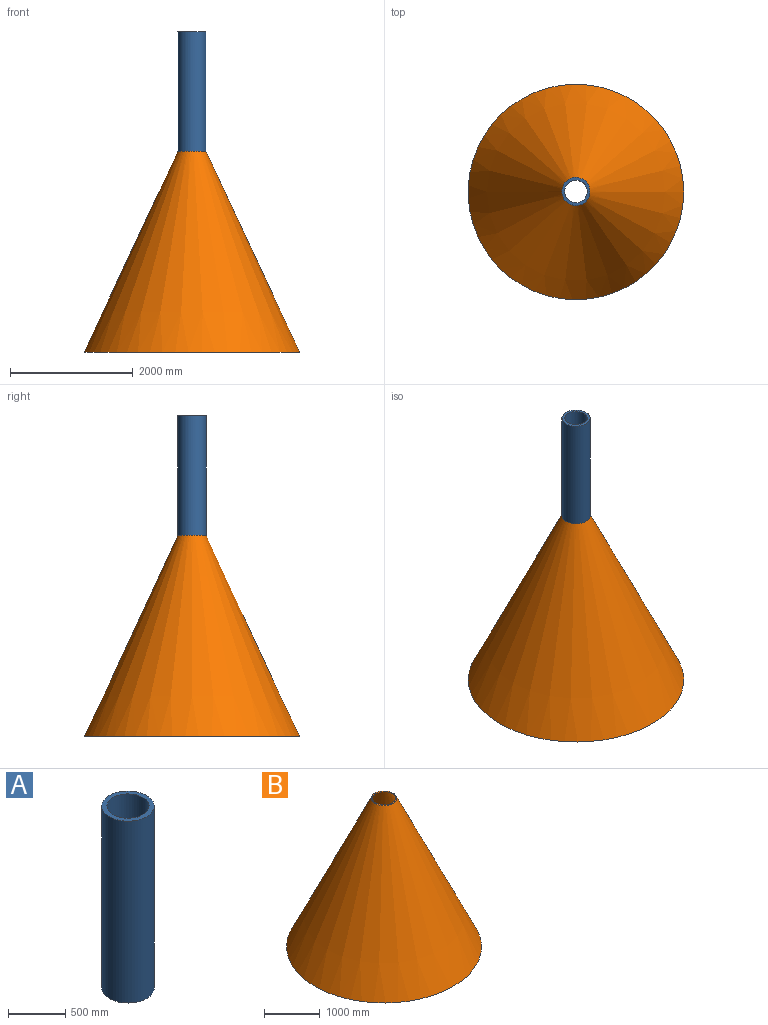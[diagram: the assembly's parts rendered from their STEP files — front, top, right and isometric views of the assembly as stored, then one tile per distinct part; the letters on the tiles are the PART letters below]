
ASSEMBLY  parts=2 mates=1
PART A: 4 faces, bbox 457.2x457.2x1945 mm
  f0: cylinder r=183.6mm len=1945mm, axis (0,0,-1), area 2243738mm2, adj f2,f3
  f1: cylinder r=228.6mm len=1945mm, axis (0,0,-1), area 2793673.8mm2, adj f2,f3
  f2: plane 457.2x457.2mm, normal (0,0,1), area 58273.4mm2, adj f0,f1
  f3: plane 457.2x457.2mm, normal (0,0,-1), area 58273.4mm2, adj f0,f1
PART B: 4 faces, bbox 3505x3505x3268 mm
  f0: cone r=1730.43mm half-angle=25deg, axis (0,0,-1), area 21942104.7mm2, adj f1,f3
  f1: plane 3505x3505mm, normal (0,0,-1), area 241462.4mm2, adj f0,f2
  f2: cone r=1752.5mm half-angle=25deg, axis (0,0,-1), area 22442071.5mm2, adj f1,f3
  f3: plane 457.2x457.2mm, normal (0,0,1), area 30166.6mm2, adj f0,f2
PLACE A t=(822.2,1577.6,681.86)mm
PLACE B t=(822.2,1577.6,-2586.14)mm
MATE fastened B.f0 <-> A.f0  axis (0,0,1) through (822.2,1577.6,681.86)mm
